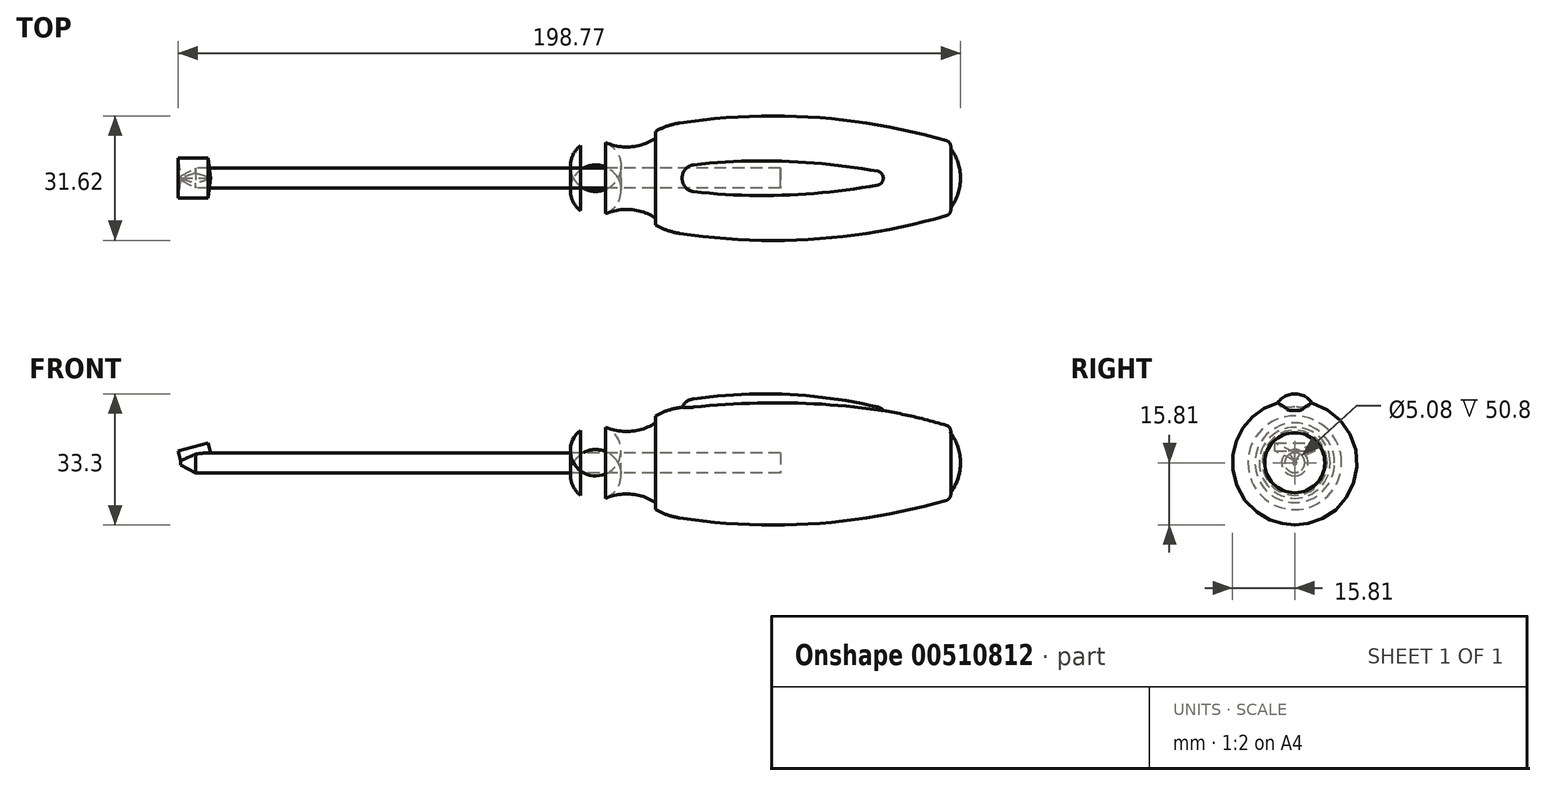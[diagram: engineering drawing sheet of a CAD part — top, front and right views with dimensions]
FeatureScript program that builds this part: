
annotation { "Feature Type Name" : "Feature", "Feature Type Description" : "" }
export const myFeature = defineFeature(function(context is Context, id is Id, definition is map)
    precondition{}
    {
        {
            var Q0;
            Q0=qCreatedBy(makeId("Front.planeOp"),FACE);
            var sketch = newSketch(context, id + "F0", { "sketchPlane" : qUnion([Q0])});
            skLineSegment(sketch, "E0", {"start": v(-101.6, 0) * mm, "end": v(96.52, 0) * mm});
            skLineSegment(sketch, "E1", {"start": v(96.52, 0) * mm, "end": v(117.55, 0) * mm, "construction": true});
            skLineSegment(sketch, "E2", {"start": v(50.8, 2.54) * mm, "end": v(-97.8, 2.54) * mm});
            skLineSegment(sketch, "E3", {"start": v(-101.6, 0.5) * mm, "end": v(-101.6, 0) * mm});
            skLineSegment(sketch, "E4", {"start": v(0, 2.54) * mm, "end": v(0, 8.25) * mm});
            skArc(sketch, "E5", {"start": v(6.35, 9.02) * mm, "mid": v(3.07, 9.48) * mm, "end": v(0, 8.25) * mm});
            skArc(sketch, "E6", {"start": v(6.35, 9.02) * mm, "mid": v(12.84, 7.99) * mm, "end": v(19.05, 10.11) * mm});
            skArc(sketch, "E7", {"start": v(25.4, 12.52) * mm, "mid": v(22.1, 11.65) * mm, "end": v(19.05, 10.11) * mm});
            skArc(sketch, "E8", {"start": v(93.98, 7.62) * mm, "mid": v(59.96, 13.9) * mm, "end": v(25.4, 12.52) * mm});
            skArc(sketch, "E9", {"start": v(96.52, 0) * mm, "mid": v(95.87, 4.02) * mm, "end": v(93.98, 7.62) * mm});
            skArc(sketch, "E10.0", {"start": v(25.17, 14.02) * mm, "mid": v(22.01, 13.24) * mm, "end": v(19.05, 11.9) * mm});
            skArc(sketch, "E10.1", {"start": v(92.95, 9.52) * mm, "mid": v(59.3, 15.46) * mm, "end": v(25.17, 14.02) * mm});
            skLineSegment(sketch, "E11", {"start": v(19.05, 11.9) * mm, "end": v(19.05, 10.11) * mm});
            skArc(sketch, "E12", {"start": v(93.98, 7.62) * mm, "mid": v(93.86, 8.78) * mm, "end": v(92.95, 9.52) * mm});
            skPoint(sketch, "E13.orphan", {"position": v(0, 0) * mm});
            skLineSegment(sketch, "E14", {"start": v(50.8, 2.54) * mm, "end": v(50.8, 0) * mm});
            skLineSegment(sketch, "E15", {"start": v(-101.6, 0.5) * mm, "end": v(-97.8, 2.54) * mm});
            skPoint(sketch, "E16.orphan", {"position": v(-101.6, 2.54) * mm});
            skSolve(sketch);
        }
        {
            var Q0;
            Q0=qCreatedBy(makeId("Front.planeOp"),FACE);
            var sketch = newSketch(context, id + "F1", { "sketchPlane" : qUnion([Q0])});
            skLineSegment(sketch, "E17", {"start": v(25.4, 12.52) * mm, "end": v(77.47, 11.64) * mm});
            skArc(sketch, "E18", {"start": v(28.67, 16.22) * mm, "mid": v(26.35, 14.97) * mm, "end": v(25.4, 12.52) * mm});
            skArc(sketch, "E19", {"start": v(77.47, 11.64) * mm, "mid": v(76.93, 13.25) * mm, "end": v(75.5, 14.16) * mm});
            skArc(sketch, "E20", {"start": v(75.5, 14.16) * mm, "mid": v(52.19, 17.37) * mm, "end": v(28.67, 16.22) * mm});
            skSolve(sketch);
        }
        {
            var Q0;
            Q0=qCreatedBy(makeId("Front.planeOp"),FACE);
            var sketch = newSketch(context, id + "F2", { "sketchPlane" : qUnion([Q0])});
            skLineSegment(sketch, "E21", {"start": v(-101.6, 0.5) * mm, "end": v(-93.98, 2.54) * mm});
            skSolve(sketch);
        }
        {
            var Q0;
            Q0=sQuery(id+"F2.wireOp",VERTEX,"E21.start");
            var Q1;
            Q1=sQuery(id+"F2.wireOp",EDGE,"E21");
            cPlane(context, id + "F3", {"entities" : qUnion([Q0, Q1]), "cplaneType" : CPlaneType.LINE_POINT, "offset" : 25.4 * mm, "width" : 152.4 * mm, "height" : 152.4 * mm});
        }
        {
            var Q0;
            Q0=qCreatedBy(id+"F3.planeOp",FACE);
            var sketch = newSketch(context, id + "F4", { "sketchPlane" : qUnion([Q0])});
            skLineSegment(sketch, "E22", {"start": v(5.08, 29.2) * mm, "end": v(0, 26.67) * mm});
            skLineSegment(sketch, "E23", {"start": v(0, 26.67) * mm, "end": v(-5.08, 29.2) * mm});
            skLineSegment(sketch, "E24", {"start": v(-5.08, 29.2) * mm, "end": v(5.08, 29.2) * mm});
            skLineSegment(sketch, "E25", {"start": v(0, 29.2) * mm, "end": v(0, 26.67) * mm, "construction": true});
            skSolve(sketch);
        }
        {
            var Q0;
            {var subQ0=sQuery(id+"F0.wireOp",EDGE,"E4");Q0=makeQuery(id+"F0.imprint","IMPRINT",FACE,{"disambiguationData":[TD([[makeQuery(id+"F0.imprint","IMPRINT",EDGE,{"derivedFrom":subQ0}),-1.0]])]});}
            var Q1;
            Q1=sQuery(id+"F0.wireOp",EDGE,"E1");
            revolve(context, id + "F5", {"entities" : qUnion([Q0]), "axis" : qUnion([Q1]), "revolveType" : RevolveType.FULL});
        }
        {
            var Q0;
            {var subQ0=sQuery(id+"F0.wireOp",EDGE,"E3");Q0=makeQuery(id+"F0.imprint","IMPRINT",FACE,{"disambiguationData":[TD([[makeQuery(id+"F0.imprint","IMPRINT",EDGE,{"derivedFrom":subQ0}),1.0]])]});}
            var Q1;
            Q1=sQuery(id+"F0.wireOp",EDGE,"E0");
            revolve(context, id + "F6", {"entities" : qUnion([Q0]), "axis" : qUnion([Q1]), "revolveType" : RevolveType.FULL});
        }
        {
            var Q0;
            Q0=makeQuery(id+"F0.imprint","IMPRINT",FACE,{"disambiguationData":[TD([[makeQuery(id+"F0.imprint","IMPRINT",EDGE,{"derivedFrom":sQuery(id+"F0.wireOp",EDGE,"E7")}),-1.0]])]});
            var Q1;
            Q1=sQuery(id+"F0.wireOp",EDGE,"E1");
            revolve(context, id + "F7", {"entities" : qUnion([Q0]), "axis" : qUnion([Q1]), "revolveType" : RevolveType.FULL});
        }
        {
            var Q0;
            Q0=makeQuery(id+"F1.imprint","IMPRINT",FACE,{"disambiguationData":[TD([[makeQuery(id+"F1.imprint","IMPRINT",EDGE,{"derivedFrom":sQuery(id+"F1.wireOp",EDGE,"E17")}),1.0]])]});
            var Q1;
            Q1=sQuery(id+"F1.wireOp",EDGE,"E17");
            revolve(context, id + "F8", {"operationType" : NewBodyOperationType.ADD, "entities" : qUnion([Q0]), "axis" : qUnion([Q1]), "revolveType" : RevolveType.FULL});
        }
        {
            var Q0;
            Q0=makeQuery(id+"F4.imprint","IMPRINT",FACE,{"disambiguationData":[TD([[makeQuery(id+"F4.imprint","IMPRINT",EDGE,{"derivedFrom":sQuery(id+"F4.wireOp",EDGE,"E22")}),-1.0]])]});
            extrude(context, id + "F9", {"entities" : qUnion([Q0]), "operationType" : NewBodyOperationType.REMOVE, "depth" : 25.4 * mm, "offsetDistance" : 25.4 * mm});
        }
        {
            var Q0;
            Q0=makeQuery(id+"F4.imprint","IMPRINT",FACE,{"disambiguationData":[TD([[makeQuery(id+"F4.imprint","IMPRINT",EDGE,{"derivedFrom":sQuery(id+"F4.wireOp",EDGE,"E22")}),-1.0]])]});
            var Q1;
            Q1=qConstructionFilter(qBodyType(qCreatedBy(id+"F2",EDGE),BodyType.WIRE),ConstructionObject.NO);
            sweep(context, id + "F10", {"profiles" : qUnion([Q0]), "path" : qUnion([Q1])});
        }
    });
